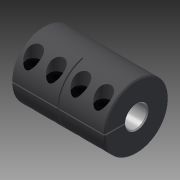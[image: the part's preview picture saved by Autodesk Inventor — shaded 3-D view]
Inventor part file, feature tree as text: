
AUTODESK INVENTOR PART (.ipt)
format: ipt  version: 2014 SP1 (Build 180222100, 222)  size: 2,163,200 bytes
history: native  units: in
note: dims shown in document units (in); Inventor stores cm internally (conversion verified against a paired STEP export)
features: other x5, imported_body x5, mirror x1
ambient origin geometry x8: Origin, YZ Plane, XZ Plane, XY Plane, X Axis, Y Axis, Z Axis, Center Point
bodies: Body1 (feature_tree), Body2 (feature_tree), Body3 (feature_tree), Body4 (feature_tree), Body5 (feature_tree)
feature tree (11):
  mirror  "Mirror1"
  other  "2469K2001"
  other  "Cut-Sweep1"
  other  "LPattern2"
  other  "LPattern3[1]"
  other  "LPattern3[2]"
  imported_body  "Base1"
  imported_body  "Base2"
  imported_body  "Base3"
  imported_body  "Base4"
  imported_body  "Base5"
